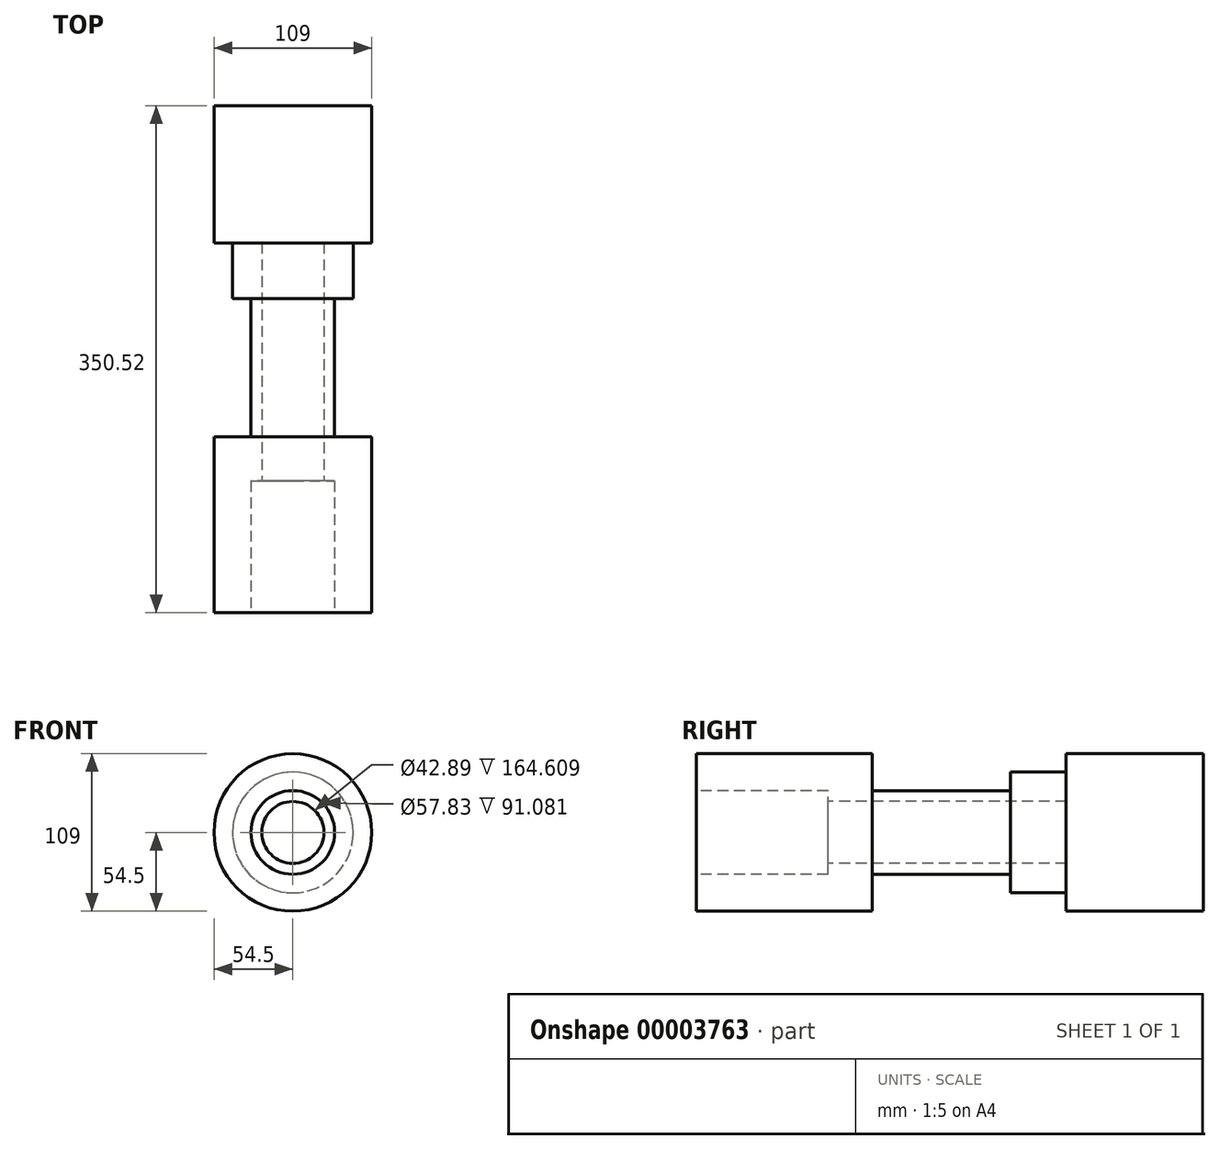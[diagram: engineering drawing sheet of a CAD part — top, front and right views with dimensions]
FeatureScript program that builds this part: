
annotation { "Feature Type Name" : "Feature", "Feature Type Description" : "" }
export const myFeature = defineFeature(function(context is Context, id is Id, definition is map)
    precondition{}
    {
        {
            var Q0;
            Q0=qCreatedBy(makeId("Front.planeOp"),FACE);
            var sketch = newSketch(context, id + "F0", { "sketchPlane" : qUnion([Q0])});
            skCircle(sketch, "E0", {"center": v(0, 0) * mm, "radius": 41.76 * mm});
            skSolve(sketch);
        }
        {
            var Q0;
            Q0=makeQuery(id+"F0.imprint","IMPRINT",FACE,{"disambiguationData":[TD([[makeQuery(id+"F0.imprint","IMPRINT",EDGE,{"derivedFrom":sQuery(id+"F0.wireOp",EDGE,"E0")}),1.0]])]});
            extrude(context, id + "F1", {"entities" : qUnion([Q0]), "depth" : 107.93 * mm});
        }
        {
            var Q0;
            Q0=makeQuery(id+"F1.opExtrude","CAP_FACE",FACE,{"disambiguationData":[OSD([sQuery(id+"F0.wireOp",EDGE,"E0")])],"isStart":false});
            var sketch = newSketch(context, id + "F2", { "sketchPlane" : qUnion([Q0])});
            skCircle(sketch, "E1", {"center": v(0, 0) * mm, "radius": 28.91 * mm});
            skSolve(sketch);
        }
        {
            var Q0;
            Q0=makeQuery(id+"F2.imprint","IMPRINT",FACE,{"disambiguationData":[TD([[makeQuery(id+"F2.imprint","IMPRINT",EDGE,{"derivedFrom":sQuery(id+"F2.wireOp",EDGE,"E1")}),1.0]])]});
            extrude(context, id + "F3", {"entities" : qUnion([Q0]), "operationType" : NewBodyOperationType.ADD, "depth" : 126.1 * mm});
        }
        {
            var Q0;
            Q0=makeQuery(id+"F3.opExtrude","CAP_FACE",FACE,{"disambiguationData":[OSD([sQuery(id+"F2.wireOp",EDGE,"E1")])],"isStart":false});
            var sketch = newSketch(context, id + "F4", { "sketchPlane" : qUnion([Q0])});
            skCircle(sketch, "E2", {"center": v(0, 0) * mm, "radius": 21.45 * mm});
            skSolve(sketch);
        }
        {
            var Q0;
            Q0=makeQuery(id+"F4.imprint","IMPRINT",FACE,{"disambiguationData":[TD([[makeQuery(id+"F4.imprint","IMPRINT",EDGE,{"derivedFrom":sQuery(id+"F4.wireOp",EDGE,"E2")}),1.0]])]});
            extrude(context, id + "F5", {"entities" : qUnion([Q0]), "operationType" : NewBodyOperationType.REMOVE, "oppositeDirection" : true, "depth" : 265.65 * mm});
        }
        {
            var Q0;
            Q0=makeQuery(id+"F3.opExtrude","CAP_FACE",FACE,{"disambiguationData":[OSD([sQuery(id+"F2.wireOp",EDGE,"E1")])],"isStart":false});
            var sketch = newSketch(context, id + "F6", { "sketchPlane" : qUnion([Q0])});
            skCircle(sketch, "E3.0", {"center": v(0, 0) * mm, "radius": 21.45 * mm});
            skCircle(sketch, "E4.0", {"center": v(0, 0) * mm, "radius": 54.5 * mm});
            skSolve(sketch);
        }
        {
            var Q0;
            Q0=makeQuery(id+"F6.imprint","IMPRINT",FACE,{"disambiguationData":[TD([[makeQuery(id+"F6.imprint","IMPRINT",EDGE,{"derivedFrom":sQuery(id+"F6.wireOp",EDGE,"E4.0")}),1.0]])]});
            var Q1;
            Q1=sQuery(id+"F6.wireOp",EDGE,"E4.0");
            extrude(context, id + "F7", {"entities" : qUnion([Q0]), "surfaceEntities" : qUnion([Q1]), "oppositeDirection" : true, "depth" : 30.46 * mm});
        }
        {
            var Q0;
            Q0=makeQuery(id+"F7.opExtrude","CAP_FACE",FACE,{"disambiguationData":[OSD([sQuery(id+"F2.wireOp",EDGE,"E1"),sQuery(id+"F6.wireOp",EDGE,"E4.0")])],"isStart":true});
            var sketch = newSketch(context, id + "F8", { "sketchPlane" : qUnion([Q0])});
            skCircle(sketch, "E5.0", {"center": v(0, 0) * mm, "radius": 54.5 * mm});
            skCircle(sketch, "E6.0", {"center": v(0, 0) * mm, "radius": 21.45 * mm});
            skSolve(sketch);
        }
        {
            var Q0;
            Q0=makeQuery(id+"F8.imprint","IMPRINT",FACE,{"disambiguationData":[TD([[makeQuery(id+"F8.imprint","IMPRINT",EDGE,{"derivedFrom":sQuery(id+"F8.wireOp",EDGE,"E5.0")}),1.0]])]});
            extrude(context, id + "F9", {"entities" : qUnion([Q0]), "operationType" : NewBodyOperationType.ADD, "depth" : 91.08 * mm});
        }
        {
            var Q0;
            Q0=makeQuery(id+"F1.opExtrude","CAP_FACE",FACE,{"disambiguationData":[OSD([sQuery(id+"F0.wireOp",EDGE,"E0")])],"isStart":true});
            var sketch = newSketch(context, id + "F10", { "sketchPlane" : qUnion([Q0])});
            skCircle(sketch, "E7.0", {"center": v(0, 0) * mm, "radius": 41.76 * mm});
            skCircle(sketch, "E8.1", {"center": v(0, 0) * mm, "radius": 21.45 * mm});
            skCircle(sketch, "E9.0", {"center": v(0, 0) * mm, "radius": 54.5 * mm});
            skSolve(sketch);
        }
        {
            var Q0;
            Q0 = qSketchRegion(id + "F10", true);
            var Q1;
            Q1=makeQuery(id+"F10.imprint","IMPRINT",FACE,{"disambiguationData":[TD([[makeQuery(id+"F10.imprint","IMPRINT",EDGE,{"derivedFrom":sQuery(id+"F10.wireOp",EDGE,"E8.1")}),-1.0]])]});
            extrude(context, id + "F11", {"entities" : qUnion([Q0, Q1]), "oppositeDirection" : true, "depth" : 69.43 * mm});
        }
        {
            var Q0;
            Q0=makeQuery(id+"F11.opExtrude","CAP_FACE",FACE,{"disambiguationData":[OSD([sQuery(id+"F10.wireOp",EDGE,"E7.0"),sQuery(id+"F10.wireOp",EDGE,"E9.0")])],"isStart":true});
            var sketch = newSketch(context, id + "F12", { "sketchPlane" : qUnion([Q0])});
            skCircle(sketch, "E10.0", {"center": v(0, 0) * mm, "radius": 54.5 * mm});
            skSolve(sketch);
        }
        {
            var Q0;
            Q0 = qSketchRegion(id + "F12", true);
            extrude(context, id + "F13", {"entities" : qUnion([Q0]), "operationType" : NewBodyOperationType.ADD, "depth" : 25.4 * mm});
        }
    });
